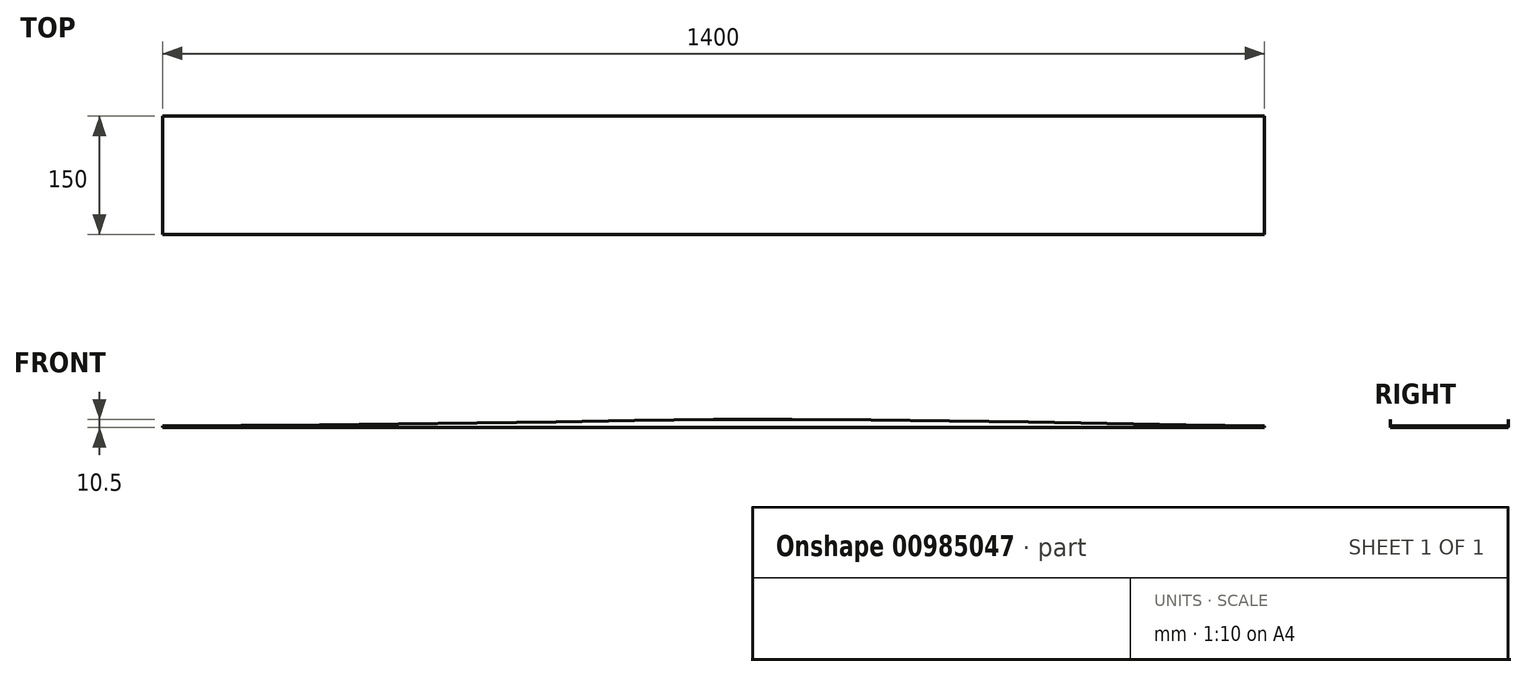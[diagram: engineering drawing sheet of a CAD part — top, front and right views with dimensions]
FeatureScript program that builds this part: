
annotation { "Feature Type Name" : "Feature", "Feature Type Description" : "" }
export const myFeature = defineFeature(function(context is Context, id is Id, definition is map)
    precondition{}
    {
        {
            var Q0;
            Q0=qCreatedBy(makeId("Front.planeOp"),FACE);
            var sketch = newSketch(context, id + "F0", { "sketchPlane" : qUnion([Q0])});
            skLineSegment(sketch, "E0", {"start": v(-700, -5.25) * mm, "end": v(-700, -3.25) * mm});
            skLineSegment(sketch, "E1", {"start": v(700, -5.25) * mm, "end": v(700, -3.25) * mm});
            skLineSegment(sketch, "E2", {"start": v(-700, -5.25) * mm, "end": v(700, -5.25) * mm});
            skLineSegment(sketch, "E3", {"start": v(-700, -3.25) * mm, "end": v(-600, -2.55) * mm});
            skLineSegment(sketch, "E4", {"start": v(-600, -2.55) * mm, "end": v(-500, -1.7) * mm});
            skLineSegment(sketch, "E5", {"start": v(-500, -1.7) * mm, "end": v(-400, -0.5) * mm});
            skLineSegment(sketch, "E6", {"start": v(-400, -0.5) * mm, "end": v(-300, 0.8) * mm});
            skLineSegment(sketch, "E7", {"start": v(-300, 0.8) * mm, "end": v(-200, 2.25) * mm});
            skLineSegment(sketch, "E8", {"start": v(-200, 2.25) * mm, "end": v(-100, 3.75) * mm});
            skLineSegment(sketch, "E9", {"start": v(-100, 3.75) * mm, "end": v(0, 4.95) * mm});
            skLineSegment(sketch, "E10", {"start": v(0, 4.95) * mm, "end": v(100, 5.25) * mm});
            skLineSegment(sketch, "E11", {"start": v(100, 5.25) * mm, "end": v(200, 4.65) * mm});
            skLineSegment(sketch, "E12", {"start": v(200, 4.65) * mm, "end": v(300, 3.4) * mm});
            skLineSegment(sketch, "E13", {"start": v(300, 3.4) * mm, "end": v(400, 1.85) * mm});
            skLineSegment(sketch, "E14", {"start": v(400, 1.85) * mm, "end": v(500, 0) * mm});
            skLineSegment(sketch, "E15", {"start": v(500, 0) * mm, "end": v(600, -2) * mm});
            skLineSegment(sketch, "E16", {"start": v(600, -2) * mm, "end": v(700, -3.25) * mm});
            skSolve(sketch);
        }
        {
            var Q0;
            Q0=makeQuery(id+"F0.imprint","IMPRINT",FACE,{"disambiguationData":[TD([[makeQuery(id+"F0.imprint","IMPRINT",EDGE,{"derivedFrom":sQuery(id+"F0.wireOp",EDGE,"E0")}),-1.0]])]});
            extrude(context, id + "F1", {"entities" : qUnion([Q0]), "depth" : 150 * mm, "offsetDistance" : 25 * mm});
        }
    });
